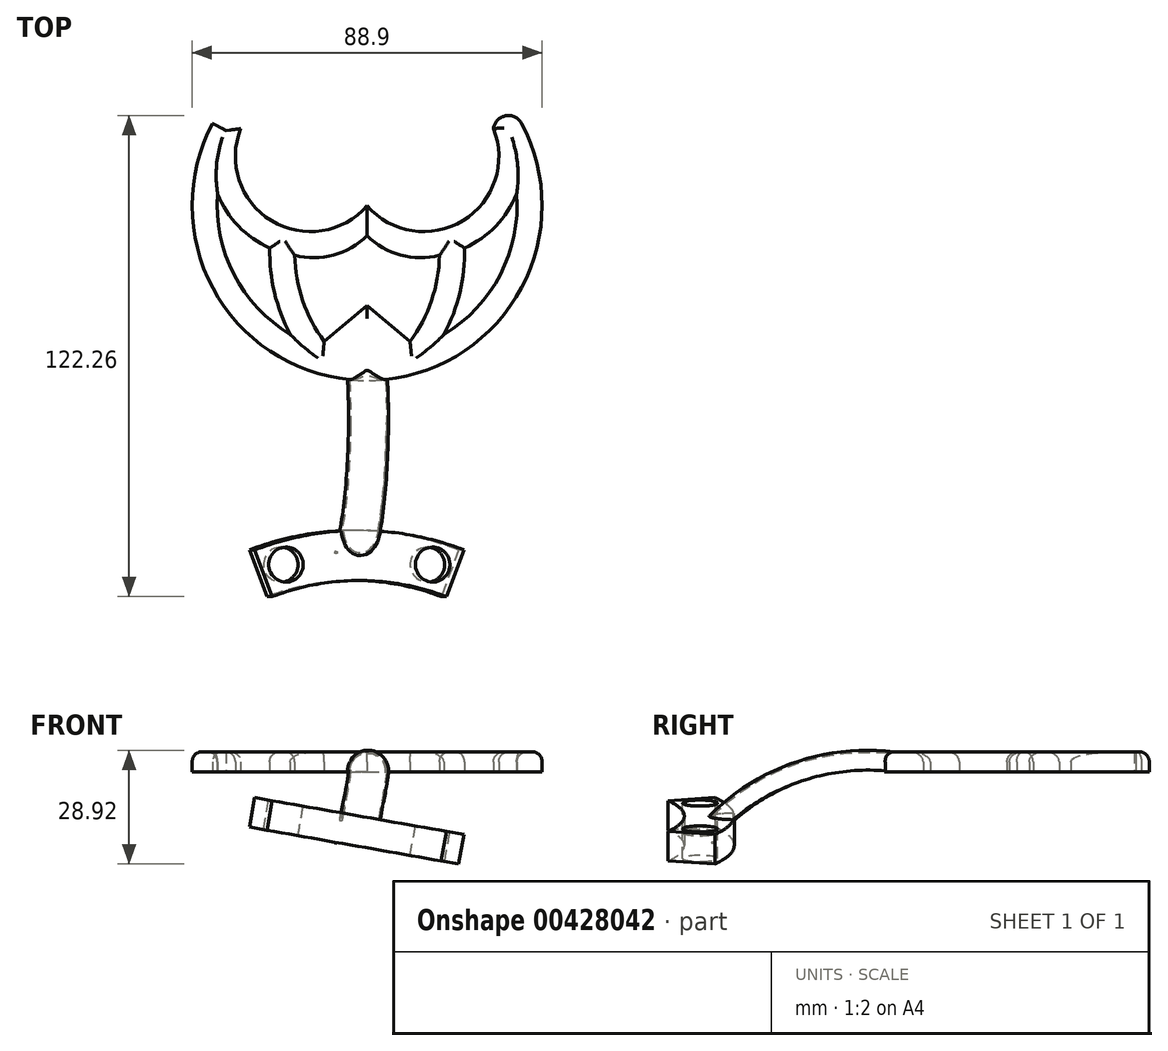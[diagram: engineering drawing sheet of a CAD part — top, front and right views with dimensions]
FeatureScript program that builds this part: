
annotation { "Feature Type Name" : "Feature", "Feature Type Description" : "" }
export const myFeature = defineFeature(function(context is Context, id is Id, definition is map)
    precondition{}
    {
        {
            var Q0;
            Q0=qCreatedBy(makeId("Top.planeOp"),FACE);
            var sketch = newSketch(context, id + "F0", { "sketchPlane" : qUnion([Q0])});
            skArc(sketch, "E0", {"start": v(-39.25, 20.86) * mm, "mid": v(0, -44.45) * mm, "end": v(39.25, 20.86) * mm});
            skPoint(sketch, "E1", {"position": v(0, -44.45) * mm});
            skArc(sketch, "E2", {"start": v(-39.25, 20.86) * mm, "mid": v(-35.2, 22.82) * mm, "end": v(-32.1, 19.54) * mm});
            skLineSegment(sketch, "E3", {"start": v(-35.88, 19.08) * mm, "end": v(-39.25, 20.86) * mm});
            skLineSegment(sketch, "E4", {"start": v(-35.88, 19.08) * mm, "end": v(-32.1, 19.54) * mm});
            skArc(sketch, "E5", {"start": v(-32.1, 19.54) * mm, "mid": v(-24.33, -3.83) * mm, "end": v(0, 0) * mm});
            skPoint(sketch, "E6", {"position": v(0, -25.4) * mm});
            skLineSegment(sketch, "E7", {"start": v(0, -44.45) * mm, "end": v(0, -25.4) * mm});
            skLineSegment(sketch, "E8", {"start": v(0, -25.4) * mm, "end": v(-18.1, -40.6) * mm});
            skArc(sketch, "E9", {"start": v(-17.99, -6.27) * mm, "mid": v(-14.76, -28.08) * mm, "end": v(0, -44.45) * mm});
            skLineSegment(sketch, "E10", {"start": v(0, 0) * mm, "end": v(0, -7.62) * mm});
            skArc(sketch, "E11", {"start": v(-18.39, -12.6) * mm, "mid": v(-8.53, -12.58) * mm, "end": v(0, -7.62) * mm});
            skArc(sketch, "E12", {"start": v(-24.73, -10.77) * mm, "mid": v(-23.55, -22.07) * mm, "end": v(-19.55, -32.7) * mm});
            skArc(sketch, "E13", {"start": v(-37.99, 2.95) * mm, "mid": v(-32.7, -5.2) * mm, "end": v(-24.73, -10.77) * mm});
            skArc(sketch, "E14", {"start": v(-37.99, 2.95) * mm, "mid": v(-33.84, -17.5) * mm, "end": v(-19.55, -32.7) * mm});
            skArc(sketch, "E15.MirrorCS", {"start": v(32.1, 19.54) * mm, "mid": v(24.33, -3.83) * mm, "end": v(0, 0) * mm});
            skArc(sketch, "E16.MirrorCS", {"start": v(39.25, 20.86) * mm, "mid": v(35.2, 22.82) * mm, "end": v(32.1, 19.54) * mm});
            skArc(sketch, "E17.MirrorCS", {"start": v(39.25, 20.86) * mm, "mid": v(0, -44.45) * mm, "end": v(-39.25, 20.86) * mm});
            skArc(sketch, "E18.MirrorCS", {"start": v(37.99, 2.95) * mm, "mid": v(33.84, -17.5) * mm, "end": v(19.55, -32.7) * mm});
            skArc(sketch, "E19.MirrorCS", {"start": v(24.73, -10.77) * mm, "mid": v(23.55, -22.07) * mm, "end": v(19.55, -32.7) * mm});
            skArc(sketch, "E20.MirrorCS", {"start": v(17.99, -6.27) * mm, "mid": v(14.76, -28.08) * mm, "end": v(0, -44.45) * mm});
            skLineSegment(sketch, "E21.MirrorCS", {"start": v(0, -25.4) * mm, "end": v(18.1, -40.6) * mm});
            skArc(sketch, "E22.MirrorCS", {"start": v(37.99, 2.95) * mm, "mid": v(32.7, -5.2) * mm, "end": v(24.73, -10.77) * mm});
            skArc(sketch, "E23.MirrorCS", {"start": v(18.39, -12.6) * mm, "mid": v(8.53, -12.58) * mm, "end": v(0, -7.62) * mm});
            skSolve(sketch);
        }
        {
            var Q0;
            Q0=makeQuery(id+"F0.imprint","IMPRINT",FACE,{"disambiguationData":[TD([[makeQuery(id+"F0.imprint","IMPRINT",EDGE,{"derivedFrom":sQuery(id+"F0.wireOp",EDGE,"E2")}),-1.0]])]});
            var Q1;
            {var subQ9=sQuery(id+"F0.wireOp",EDGE,"E3");Q1=makeQuery(id+"F0.imprint","IMPRINT",FACE,{"disambiguationData":[TD([[makeQuery(id+"F0.imprint","IMPRINT",EDGE,{"derivedFrom":subQ9}),1.0]])]});}
            var Q2;
            {var subQ0=sQuery(id+"F0.wireOp",EDGE,"E10");Q2=makeQuery(id+"F0.imprint","IMPRINT",FACE,{"disambiguationData":[TD([[makeQuery(id+"F0.imprint","IMPRINT",EDGE,{"derivedFrom":subQ0}),-1.0]])]});}
            var Q3;
            {var subQ0=sQuery(id+"F0.wireOp",EDGE,"E10");Q3=makeQuery(id+"F0.imprint","IMPRINT",FACE,{"disambiguationData":[TD([[makeQuery(id+"F0.imprint","IMPRINT",EDGE,{"derivedFrom":subQ0}),1.0]])]});}
            var Q4;
            {var subQ0=sQuery(id+"F0.wireOp",EDGE,"E7");Q4=makeQuery(id+"F0.imprint","IMPRINT",FACE,{"disambiguationData":[TD([[makeQuery(id+"F0.imprint","IMPRINT",EDGE,{"derivedFrom":subQ0}),1.0]])]});}
            var Q5;
            {var subQ0=sQuery(id+"F0.wireOp",EDGE,"E17.MirrorCS");var subQ1=sQuery(id+"F0.wireOp",EDGE,"E8");var subQ2=makeQuery(id+"F0.imprint","INTERSECT",VERTEX,{"derivedFrom":[subQ1,subQ0]});Q5=makeQuery(id+"F0.imprint","IMPRINT",FACE,{"disambiguationData":[TD([[makeQuery(id+"F0.imprint","IMPRINT",EDGE,{"disambiguationData":[TD([[subQ2,1.0]])],"derivedFrom":subQ1}),1.0]])]});}
            var Q6;
            {var subQ0=sQuery(id+"F0.wireOp",EDGE,"E7");Q6=makeQuery(id+"F0.imprint","IMPRINT",FACE,{"disambiguationData":[TD([[makeQuery(id+"F0.imprint","IMPRINT",EDGE,{"derivedFrom":subQ0}),-1.0]])]});}
            var Q7;
            {var subQ1=sQuery(id+"F0.wireOp",EDGE,"E17.MirrorCS");var subQ3=sQuery(id+"F0.wireOp",EDGE,"E21.MirrorCS");var subQ4=makeQuery(id+"F0.imprint","INTERSECT",VERTEX,{"derivedFrom":[subQ1,subQ3]});Q7=makeQuery(id+"F0.imprint","IMPRINT",FACE,{"disambiguationData":[TD([[makeQuery(id+"F0.imprint","IMPRINT",EDGE,{"disambiguationData":[TD([[subQ4,1.0]])],"derivedFrom":subQ3}),-1.0]])]});}
            var Q8;
            {var subQ1=sQuery(id+"F0.wireOp",EDGE,"E16.MirrorCS");Q8=makeQuery(id+"F0.imprint","IMPRINT",FACE,{"disambiguationData":[TD([[makeQuery(id+"F0.imprint","IMPRINT",EDGE,{"derivedFrom":subQ1}),1.0]])]});}
            extrude(context, id + "F1", {"entities" : qUnion([Q0, Q1, Q2, Q3, Q4, Q5, Q6, Q7, Q8]), "depth" : 5.08 * mm});
        }
        {
            var Q0;
            Q0=makeQuery(id+"F1.opExtrude","CAP_EDGE",EDGE,{"disambiguationData":[OSD([sQuery(id+"F0.wireOp",EDGE,"E5")])],"isStart":false});
            var Q1;
            Q1=makeQuery(id+"F1.opExtrude","CAP_EDGE",EDGE,{"disambiguationData":[OSD([sQuery(id+"F0.wireOp",EDGE,"E15.MirrorCS")])],"isStart":false});
            var Q2;
            Q2=makeQuery(id+"F1.opExtrude","CAP_EDGE",EDGE,{"disambiguationData":[OSD([sQuery(id+"F0.wireOp",EDGE,"E2")])],"isStart":false});
            var Q3;
            Q3=makeQuery(id+"F1.opExtrude","CAP_EDGE",EDGE,{"disambiguationData":[OSD([sQuery(id+"F0.wireOp",EDGE,"E17.MirrorCS")])],"isStart":false});
            var Q4;
            Q4=makeQuery(id+"F1.opExtrude","CAP_EDGE",EDGE,{"disambiguationData":[OSD([sQuery(id+"F0.wireOp",EDGE,"E16.MirrorCS")])],"isStart":false});
            var Q5;
            Q5=makeQuery(id+"F1.opExtrude","CAP_EDGE",EDGE,{"disambiguationData":[OSD([sQuery(id+"F0.wireOp",EDGE,"E13")])],"isStart":false});
            var Q6;
            Q6=makeQuery(id+"F1.opExtrude","CAP_EDGE",EDGE,{"disambiguationData":[OSD([sQuery(id+"F0.wireOp",EDGE,"E14")])],"isStart":false});
            var Q7;
            Q7=makeQuery(id+"F1.opExtrude","CAP_EDGE",EDGE,{"disambiguationData":[OSD([sQuery(id+"F0.wireOp",EDGE,"E12")])],"isStart":false});
            var Q8;
            Q8=makeQuery(id+"F1.opExtrude","CAP_EDGE",EDGE,{"disambiguationData":[OSD([sQuery(id+"F0.wireOp",EDGE,"E11")])],"isStart":false});
            var Q9;
            Q9=makeQuery(id+"F1.opExtrude","CAP_EDGE",EDGE,{"disambiguationData":[OSD([sQuery(id+"F0.wireOp",EDGE,"E9")])],"isStart":false});
            var Q10;
            Q10=makeQuery(id+"F1.opExtrude","CAP_EDGE",EDGE,{"disambiguationData":[OSD([sQuery(id+"F0.wireOp",EDGE,"E8")])],"isStart":false});
            var Q11;
            Q11=makeQuery(id+"F1.opExtrude","CAP_EDGE",EDGE,{"disambiguationData":[OSD([sQuery(id+"F0.wireOp",EDGE,"E21.MirrorCS")])],"isStart":false});
            var Q12;
            Q12=makeQuery(id+"F1.opExtrude","CAP_EDGE",EDGE,{"disambiguationData":[OSD([sQuery(id+"F0.wireOp",EDGE,"E23.MirrorCS")])],"isStart":false});
            var Q13;
            Q13=makeQuery(id+"F1.opExtrude","CAP_EDGE",EDGE,{"disambiguationData":[OSD([sQuery(id+"F0.wireOp",EDGE,"E20.MirrorCS")])],"isStart":false});
            var Q14;
            Q14=makeQuery(id+"F1.opExtrude","CAP_EDGE",EDGE,{"disambiguationData":[OSD([sQuery(id+"F0.wireOp",EDGE,"E19.MirrorCS")])],"isStart":false});
            var Q15;
            Q15=makeQuery(id+"F1.opExtrude","CAP_EDGE",EDGE,{"disambiguationData":[OSD([sQuery(id+"F0.wireOp",EDGE,"E22.MirrorCS")])],"isStart":false});
            var Q16;
            Q16=makeQuery(id+"F1.opExtrude","CAP_EDGE",EDGE,{"disambiguationData":[OSD([sQuery(id+"F0.wireOp",EDGE,"E18.MirrorCS")])],"isStart":false});
            fillet(context, id + "F2", {"entities" : qUnion([Q0, Q1, Q2, Q3, Q4, Q5, Q6, Q7, Q8, Q9, Q10, Q11, Q12, Q13, Q14, Q15, Q16]), "radius" : 2.54 * mm, "tangentPropagation" : true, "allowEdgeOverflow" : false});
        }
        {
            var Q0;
            Q0=qCreatedBy(makeId("Front.planeOp"),FACE);
            cPlane(context, id + "F3", {"entities" : qUnion([Q0]), "cplaneType" : CPlaneType.OFFSET, "offset" : 41.9 * mm, "width" : 152.4 * mm, "height" : 152.4 * mm});
        }
        {
            var Q0;
            Q0=qCreatedBy(id+"F3.planeOp",FACE);
            var sketch = newSketch(context, id + "F4", { "sketchPlane" : qUnion([Q0])});
            skArc(sketch, "E24", {"start": v(5.08, 0) * mm, "mid": v(0, 5.08) * mm, "end": v(-5.08, 0) * mm});
            skArc(sketch, "E25.0", {"start": v(4.57, 0) * mm, "mid": v(0, 4.57) * mm, "end": v(-4.57, 0) * mm});
            skLineSegment(sketch, "E26", {"start": v(-5.08, 0) * mm, "end": v(-4.57, 0) * mm});
            skLineSegment(sketch, "E27", {"start": v(4.57, 0) * mm, "end": v(5.08, 0) * mm});
            skSolve(sketch);
        }
        {
            var Q0;
            Q0=sQuery(id+"F0.wireOp",EDGE,"E7");
            cPlane(context, id + "F5", {"entities" : qUnion([Q0]), "cplaneType" : CPlaneType.LINE_ANGLE, "offset" : 25.4 * mm, "angle" : 10 * degree, "width" : 152.4 * mm, "height" : 152.4 * mm});
        }
        {
            var Q0;
            Q0=qCreatedBy(id+"F5.planeOp",FACE);
            cPlane(context, id + "F6", {"entities" : qUnion([Q0]), "cplaneType" : CPlaneType.OFFSET, "offset" : 19.05 * mm, "oppositeDirection" : true, "width" : 152.4 * mm, "height" : 152.4 * mm});
        }
        {
            var Q0;
            Q0=qCreatedBy(id+"F6.planeOp",FACE);
            var sketch = newSketch(context, id + "F7", { "sketchPlane" : qUnion([Q0])});
            skArc(sketch, "E28", {"start": v(26.99, -87.49) * mm, "mid": v(0, -82.55) * mm, "end": v(-26.99, -87.49) * mm});
            skArc(sketch, "E29.0", {"start": v(22.49, -99.37) * mm, "mid": v(0, -95.25) * mm, "end": v(-22.49, -99.37) * mm});
            skPoint(sketch, "E30", {"position": v(0, -82.55) * mm});
            skLineSegment(sketch, "E31", {"start": v(-26.99, -87.49) * mm, "end": v(-22.49, -99.37) * mm});
            skLineSegment(sketch, "E32", {"start": v(26.99, -87.49) * mm, "end": v(22.49, -99.37) * mm});
            skSolve(sketch);
        }
        {
            var Q0;
            Q0=sQuery(id+"F7.wireOp",EDGE,"E28");
            cPoint(context, id + "F8", {"entities" : qUnion([Q0]), "parameter" : 0.5});
        }
        {
            var Q0;
            Q0=makeQuery(id+"F2.opFillet","BLEND_EDGE",EDGE,{"blendedFrom":[makeQuery(id+"F1.opExtrude","CAP_EDGE",EDGE,{"disambiguationData":[OSD([sQuery(id+"F0.wireOp",EDGE,"E5")])],"isStart":false}),makeQuery(id+"F1.opExtrude","CAP_EDGE",EDGE,{"disambiguationData":[OSD([sQuery(id+"F0.wireOp",EDGE,"E15.MirrorCS")])],"isStart":false})],"blendedInto":[]});
            cPoint(context, id + "F9", {"entities" : qUnion([Q0]), "parameter" : 0.5});
        }
        {
            var Q0;
            Q0 = qCreatedBy(id + "F8" ,VERTEX);
            var Q1;
            Q1=sQuery(id+"F4.wireOp",VERTEX,"E25.0.center");
            var Q2;
            Q2 = qCreatedBy(id + "F9" ,VERTEX);
            cPlane(context, id + "F10", {"entities" : qUnion([Q0, Q1, Q2]), "cplaneType" : CPlaneType.THREE_POINT, "offset" : 25.4 * mm, "width" : 152.4 * mm, "height" : 152.4 * mm});
        }
        {
            var Q0;
            Q0=qCreatedBy(id+"F10.planeOp",FACE);
            var sketch = newSketch(context, id + "F11", { "sketchPlane" : qUnion([Q0])});
            skArc(sketch, "E33", {"start": v(-41.9, 0) * mm, "mid": v(-67.94, -3.23) * mm, "end": v(-88.9, -19.02) * mm});
            skSolve(sketch);
        }
        {
            var Q0;
            Q0=makeQuery(id+"F4.imprint","IMPRINT",FACE,{"disambiguationData":[TD([[makeQuery(id+"F4.imprint","IMPRINT",EDGE,{"derivedFrom":sQuery(id+"F4.wireOp",EDGE,"E24")}),1.0]])]});
            var Q1;
            Q1=sQuery(id+"F11.wireOp",EDGE,"E33");
            sweep(context, id + "F12", {"operationType" : NewBodyOperationType.ADD, "profiles" : qUnion([Q0]), "path" : qUnion([Q1])});
        }
        {
            var Q0;
            Q0=makeQuery(id+"F7.imprint","IMPRINT",FACE,{"disambiguationData":[TD([[makeQuery(id+"F7.imprint","IMPRINT",EDGE,{"derivedFrom":sQuery(id+"F7.wireOp",EDGE,"E28")}),1.0]])]});
            extrude(context, id + "F13", {"entities" : qUnion([Q0]), "operationType" : NewBodyOperationType.ADD, "depth" : 7.62 * mm});
        }
        {
            var Q0;
            {var subQ0=sQuery(id+"F7.wireOp",EDGE,"E29.0");var subQ2=sQuery(id+"F7.wireOp",EDGE,"E28");var subQ3=sQuery(id+"F7.wireOp",EDGE,"E32");var subQ4=sQuery(id+"F7.wireOp",EDGE,"E31");Q0=makeQuery(id+"F13.boolean.opBoolean","SPLIT",FACE,{"disambiguationData":[TD([makeQuery(id+"F13.opExtrude","SWEPT_FACE",FACE,{"disambiguationData":[OSD([subQ0])]})])],"derivedFrom":makeQuery(id+"F13.opExtrude","CAP_FACE",FACE,{"disambiguationData":[OSD([subQ2,subQ0,subQ4,subQ3])],"isStart":false})});}
            var sketch = newSketch(context, id + "F14", { "sketchPlane" : qUnion([Q0])});
            skCircle(sketch, "E34", {"center": v(-18.92, -91.22) * mm, "radius": 4.45 * mm});
            skCircle(sketch, "E35", {"center": v(18.92, -91.22) * mm, "radius": 4.45 * mm});
            skSolve(sketch);
        }
        {
            var Q0;
            Q0 = qSketchRegion(id + "F14", true);
            extrude(context, id + "F15", {"entities" : qUnion([Q0]), "operationType" : NewBodyOperationType.REMOVE, "oppositeDirection" : true, "depth" : 25.4 * mm});
        }
    });
